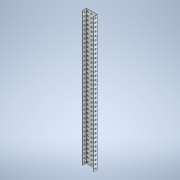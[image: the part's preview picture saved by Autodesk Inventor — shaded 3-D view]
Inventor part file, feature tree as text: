
AUTODESK INVENTOR PART (.ipt)
format: ipt  version: 2020 (Build 240168000, 168)  size: 1,396,224 bytes
history: native  units: in
note: dims shown in document units (in); Inventor stores cm internally (conversion verified against a paired STEP export)
features: other x105, plane x2, pattern_linear x1, sheet_metal_op x1
ambient origin geometry x8: Origin, YZ Plane, XZ Plane, XY Plane, X Axis, Y Axis, Z Axis, Center Point
bodies: Solid1 (feature_tree)
feature tree (109):
  other  "Work Axis1"
  pattern_linear  "Rectangular Pattern1"  Count1=35 Spacing1=0.5in
  plane  "Work Plane1"
  plane  "Work Plane2"
  other  "Work Axis2"
  other  "Work Axis3"
  other  "Work Axis4"
  other  "Work Axis5"
  other  "Work Axis6"
  other  "Work Axis7"
  other  "Work Axis8"
  other  "Work Axis9"
  other  "Work Axis10"
  other  "Work Axis11"
  other  "Work Axis12"
  other  "Work Axis13"
  other  "Work Axis14"
  other  "Work Axis15"
  other  "Work Axis16"
  other  "Work Axis17"
  other  "Work Axis18"
  other  "Work Axis19"
  other  "Work Axis20"
  other  "Work Axis21"
  other  "Work Axis22"
  other  "Work Axis23"
  other  "Work Axis24"
  other  "Work Axis25"
  other  "Work Axis26"
  other  "Work Axis27"
  other  "Work Axis28"
  other  "Work Axis29"
  other  "Work Axis30"
  other  "Work Axis31"
  other  "Work Axis32"
  other  "Work Axis33"
  other  "Work Axis34"
  other  "Work Axis35"
  other  "Work Axis36"
  other  "Work Axis37"
  other  "Work Axis38"
  other  "Work Axis39"
  other  "Work Axis40"
  other  "Work Axis41"
  other  "Work Axis42"
  other  "Work Axis43"
  other  "Work Axis44"
  other  "Work Axis45"
  other  "Work Axis46"
  other  "Work Axis47"
  other  "Work Axis48"
  other  "Work Axis49"
  other  "Work Axis50"
  other  "Work Axis51"
  other  "Work Axis52"
  other  "Work Axis53"
  other  "Work Axis54"
  other  "Work Axis55"
  other  "Work Axis56"
  other  "Work Axis57"
  other  "Work Axis58"
  other  "Work Axis59"
  other  "Work Axis60"
  other  "Work Axis61"
  other  "Work Axis62"
  other  "Work Axis63"
  other  "Work Axis64"
  other  "Work Axis65"
  other  "Work Axis66"
  other  "Work Axis67"
  other  "Work Axis68"
  other  "Work Axis69"
  other  "Work Axis70"
  other  "Work Axis71"
  other  "Work Axis72"
  other  "Work Axis73"
  other  "Work Axis74"
  other  "Work Axis75"
  other  "Work Axis76"
  other  "Work Axis77"
  other  "Work Axis78"
  other  "Work Axis79"
  other  "Work Axis80"
  other  "Work Axis81"
  other  "Work Axis82"
  other  "Work Axis83"
  other  "Work Axis84"
  other  "Work Axis85"
  other  "Work Axis86"
  other  "Work Axis87"
  other  "Work Axis88"
  other  "Work Axis89"
  other  "Work Axis90"
  other  "Work Axis91"
  other  "Work Axis92"
  other  "Work Axis93"
  other  "Work Axis94"
  other  "Work Axis95"
  other  "Work Axis96"
  other  "Work Axis97"
  other  "Work Axis98"
  other  "Work Axis99"
  other  "Work Axis100"
  other  "Work Axis101"
  other  "Work Axis102"
  other  "Work Axis103"
  other  "Work Axis104"
  other  "Work Axis105"
  sheet_metal_op  "Fold1"
